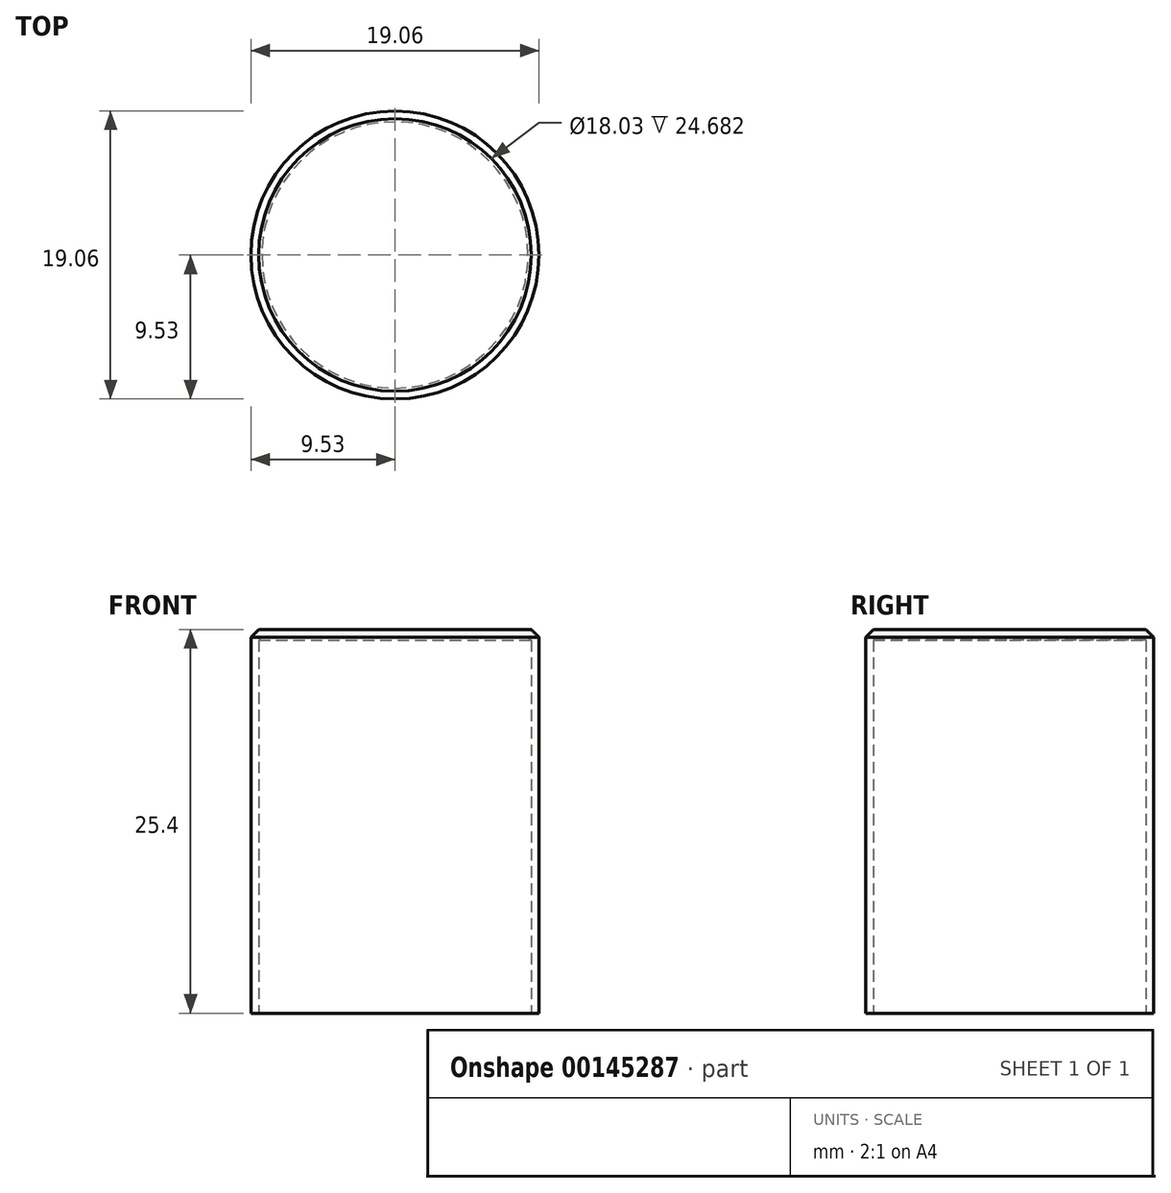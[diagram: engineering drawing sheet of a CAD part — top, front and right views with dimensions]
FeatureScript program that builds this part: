
annotation { "Feature Type Name" : "Feature", "Feature Type Description" : "" }
export const myFeature = defineFeature(function(context is Context, id is Id, definition is map)
    precondition{}
    {
        {
            var Q0;
            Q0=qCreatedBy(makeId("Top.planeOp"),FACE);
            var sketch = newSketch(context, id + "F0", { "sketchPlane" : qUnion([Q0])});
            skCircle(sketch, "E0", {"center": v(0, 0) * mm, "radius": 9.53 * mm});
            skSolve(sketch);
        }
        {
            var Q0;
            Q0=makeQuery(id+"F0.imprint","IMPRINT",FACE,{"disambiguationData":[TD([[makeQuery(id+"F0.imprint","IMPRINT",EDGE,{"derivedFrom":sQuery(id+"F0.wireOp",EDGE,"E0")}),1.0]])]});
            extrude(context, id + "F1", {"entities" : qUnion([Q0]), "depth" : 25.4 * mm});
        }
        {
            var Q0;
            Q0=makeQuery(id+"F1.opExtrude","CAP_EDGE",EDGE,{"disambiguationData":[OSD([sQuery(id+"F0.wireOp",EDGE,"E0")])],"isStart":false});
            chamfer(context, id + "F2", {"entities" : qUnion([Q0]), "width" : 0.5 * mm, "tangentPropagation" : true});
        }
        {
            var Q0;
            Q0=makeQuery(id+"F1.opExtrude","CAP_FACE",FACE,{"disambiguationData":[OSD([sQuery(id+"F0.wireOp",EDGE,"E0")])],"isStart":true});
            shell(context, id + "F3", {"entities" : qUnion([Q0]), "thickness" : 0.5 * mm});
        }
    });
